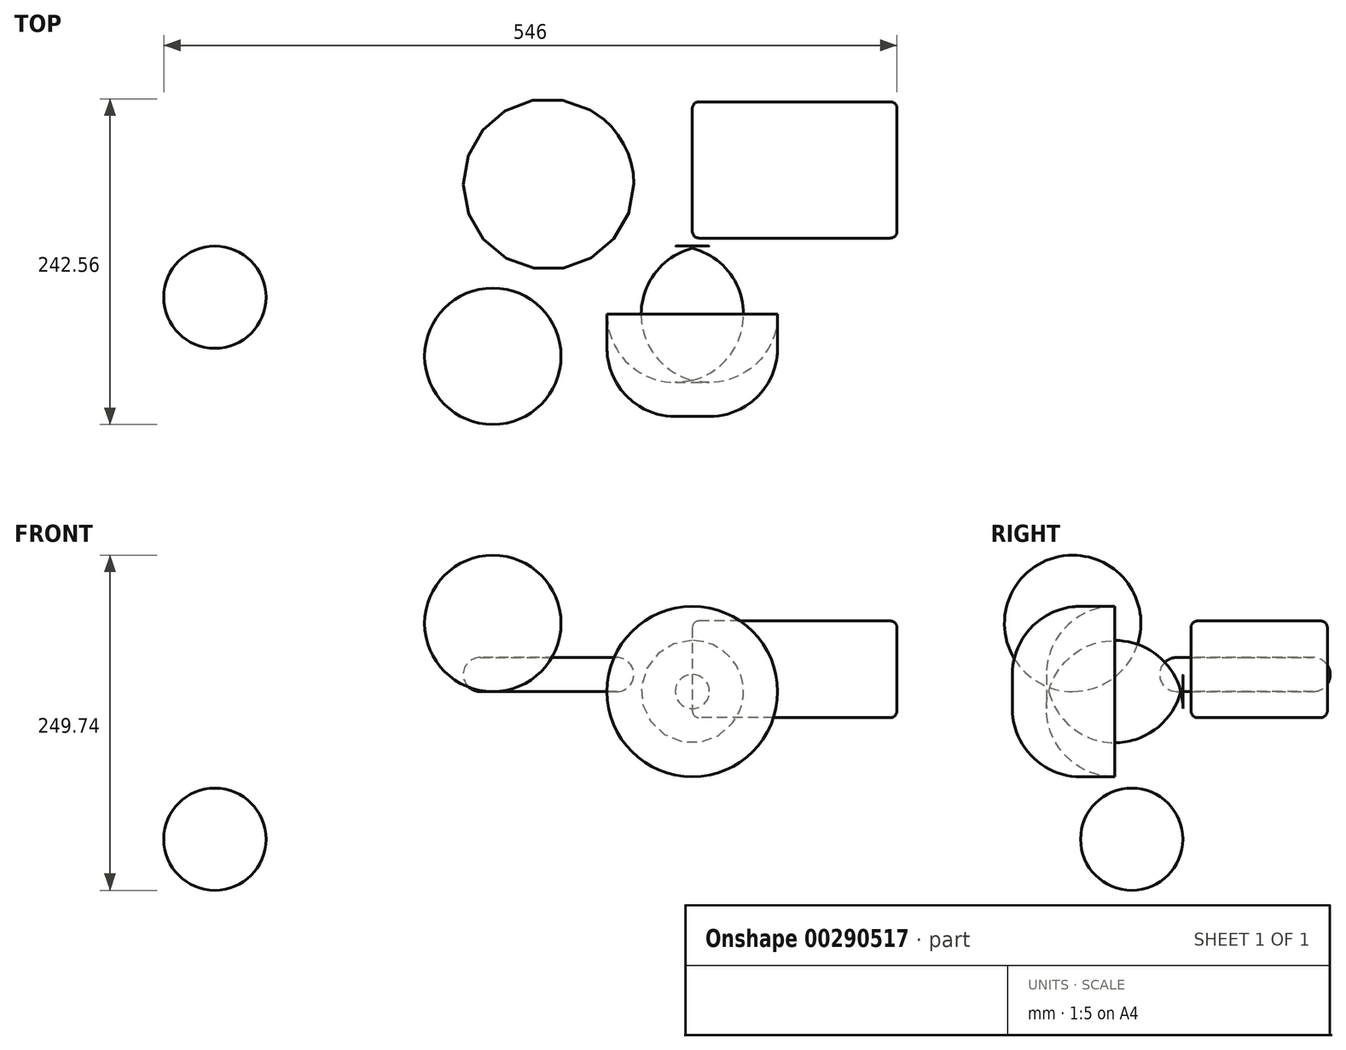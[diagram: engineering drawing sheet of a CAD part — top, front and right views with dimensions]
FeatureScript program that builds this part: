
annotation { "Feature Type Name" : "Feature", "Feature Type Description" : "" }
export const myFeature = defineFeature(function(context is Context, id is Id, definition is map)
    precondition{}
    {
        {
            var Q0;
            Q0=qCreatedBy(makeId("Front.planeOp"),FACE);
            var sketch = newSketch(context, id + "F0", { "sketchPlane" : qUnion([Q0])});
            skCircle(sketch, "E0", {"center": v(0, 0) * mm, "radius": 63.5 * mm});
            skSolve(sketch);
        }
        {
            var Q0;
            Q0=makeQuery(id+"F0.imprint","IMPRINT",FACE,{"disambiguationData":[TD([[makeQuery(id+"F0.imprint","IMPRINT",EDGE,{"derivedFrom":sQuery(id+"F0.wireOp",EDGE,"E0")}),1.0]])]});
            extrude(context, id + "F1", {"entities" : qUnion([Q0]), "depth" : 127 * mm});
        }
        {
            var Q0;
            Q0=makeQuery(id+"F1.opExtrude","CAP_FACE",FACE,{"disambiguationData":[OSD([sQuery(id+"F0.wireOp",EDGE,"E0")])],"isStart":false});
            fillet(context, id + "F2", {"entities" : qUnion([Q0]), "radius" : 50.8 * mm, "tangentPropagation" : true, "allowEdgeOverflow" : false});
        }
        {
            var Q0;
            Q0=makeQuery(id+"F1.opExtrude","CAP_FACE",FACE,{"disambiguationData":[OSD([sQuery(id+"F0.wireOp",EDGE,"E0")])],"isStart":true});
            fillet(context, id + "F3", {"entities" : qUnion([Q0]), "radius" : 50.8 * mm, "tangentPropagation" : true, "allowEdgeOverflow" : false});
        }
        {
            var Q0;
            Q0=qCreatedBy(makeId("Right.planeOp"),FACE);
            var sketch = newSketch(context, id + "F4", { "sketchPlane" : qUnion([Q0])});
            skLineSegment(sketch, "E1.bottom", {"start": v(5.96, 52.64) * mm, "end": v(107.56, 52.64) * mm});
            skLineSegment(sketch, "E1.top", {"start": v(5.96, -19.44) * mm, "end": v(107.56, -19.44) * mm});
            skLineSegment(sketch, "E1.left", {"start": v(5.96, 52.64) * mm, "end": v(5.96, -19.44) * mm});
            skLineSegment(sketch, "E1.right", {"start": v(107.56, 52.64) * mm, "end": v(107.56, -19.44) * mm});
            skSolve(sketch);
        }
        {
            var Q0;
            Q0=makeQuery(id+"F4.imprint","IMPRINT",FACE,{"disambiguationData":[TD([[makeQuery(id+"F4.imprint","IMPRINT",EDGE,{"derivedFrom":sQuery(id+"F4.wireOp",EDGE,"E1.bottom")}),-1.0]])]});
            extrude(context, id + "F5", {"entities" : qUnion([Q0]), "depth" : 152.4 * mm});
        }
        {
            var Q0;
            Q0=makeQuery(id+"F5.opExtrude","CAP_FACE",FACE,{"disambiguationData":[OSD([sQuery(id+"F4.wireOp",EDGE,"E1.bottom"),sQuery(id+"F4.wireOp",EDGE,"E1.top"),sQuery(id+"F4.wireOp",EDGE,"E1.left"),sQuery(id+"F4.wireOp",EDGE,"E1.right")])],"isStart":false});
            fillet(context, id + "F6", {"entities" : qUnion([Q0]), "radius" : 5.08 * mm, "tangentPropagation" : true, "allowEdgeOverflow" : false});
        }
        {
            var Q0;
            Q0=makeQuery(id+"F5.opExtrude","SWEPT_FACE",FACE,{"disambiguationData":[OSD([sQuery(id+"F4.wireOp",EDGE,"E1.bottom")])]});
            fillet(context, id + "F7", {"entities" : qUnion([Q0]), "radius" : 5.08 * mm, "tangentPropagation" : true, "allowEdgeOverflow" : false});
        }
        {
            var Q0;
            Q0=makeQuery(id+"F5.opExtrude","SWEPT_FACE",FACE,{"disambiguationData":[OSD([sQuery(id+"F4.wireOp",EDGE,"E1.left")])]});
            fillet(context, id + "F8", {"entities" : qUnion([Q0]), "radius" : 5.08 * mm, "tangentPropagation" : true, "allowEdgeOverflow" : false});
        }
        {
            var Q0;
            Q0=makeQuery(id+"F5.opExtrude","SWEPT_FACE",FACE,{"disambiguationData":[OSD([sQuery(id+"F4.wireOp",EDGE,"E1.top")])]});
            fillet(context, id + "F9", {"entities" : qUnion([Q0]), "radius" : 5.08 * mm, "tangentPropagation" : true, "allowEdgeOverflow" : false});
        }
        {
            var Q0;
            Q0=makeQuery(id+"F5.opExtrude","SWEPT_FACE",FACE,{"disambiguationData":[OSD([sQuery(id+"F4.wireOp",EDGE,"E1.right")])]});
            fillet(context, id + "F10", {"entities" : qUnion([Q0]), "radius" : 5.08 * mm, "tangentPropagation" : true, "allowEdgeOverflow" : false});
        }
        {
            var Q0;
            Q0=qCreatedBy(makeId("Top.planeOp"),FACE);
            var sketch = newSketch(context, id + "F11", { "sketchPlane" : qUnion([Q0])});
            skCircle(sketch, "E2", {"center": v(-107.1, 46.15) * mm, "radius": 63.5 * mm});
            skSolve(sketch);
        }
        {
            var Q0;
            Q0=makeQuery(id+"F11.imprint","IMPRINT",FACE,{"disambiguationData":[TD([[makeQuery(id+"F11.imprint","IMPRINT",EDGE,{"derivedFrom":sQuery(id+"F11.wireOp",EDGE,"E2")}),1.0]])]});
            extrude(context, id + "F12", {"entities" : qUnion([Q0]), "depth" : 25.4 * mm});
        }
        {
            var Q0;
            Q0=makeQuery(id+"F12.opExtrude","CAP_FACE",FACE,{"disambiguationData":[OSD([sQuery(id+"F11.wireOp",EDGE,"E2")])],"isStart":true});
            fillet(context, id + "F13", {"entities" : qUnion([Q0]), "radius" : 12.7 * mm, "tangentPropagation" : true, "allowEdgeOverflow" : false});
        }
        {
            var Q0;
            Q0=makeQuery(id+"F12.opExtrude","CAP_FACE",FACE,{"disambiguationData":[OSD([sQuery(id+"F11.wireOp",EDGE,"E2")])],"isStart":false});
            fillet(context, id + "F14", {"entities" : qUnion([Q0]), "radius" : 12.7 * mm, "tangentPropagation" : true, "allowEdgeOverflow" : false});
        }
        {
            var Q0;
            Q0=qCreatedBy(makeId("Top.planeOp"),FACE);
            var sketch = newSketch(context, id + "F15", { "sketchPlane" : qUnion([Q0])});
            skCircle(sketch, "E3", {"center": v(-148.55, -82.1) * mm, "radius": 50.8 * mm});
            skSolve(sketch);
        }
        {
            var Q0;
            Q0=makeQuery(id+"F15.imprint","IMPRINT",FACE,{"disambiguationData":[TD([[makeQuery(id+"F15.imprint","IMPRINT",EDGE,{"derivedFrom":sQuery(id+"F15.wireOp",EDGE,"E3")}),1.0]])]});
            extrude(context, id + "F16", {"entities" : qUnion([Q0]), "depth" : 101.6 * mm});
        }
        {
            var Q0;
            Q0=makeQuery(id+"F16.opExtrude","CAP_FACE",FACE,{"disambiguationData":[OSD([sQuery(id+"F15.wireOp",EDGE,"E3")])],"isStart":false});
            var Q1;
            Q1=makeQuery(id+"F16.opExtrude","SWEPT_FACE",FACE,{"disambiguationData":[OSD([sQuery(id+"F15.wireOp",EDGE,"E3")])]});
            fillet(context, id + "F17", {"entities" : qUnion([Q0, Q1]), "radius" : 50.8 * mm, "tangentPropagation" : true, "allowEdgeOverflow" : false});
        }
        {
            var Q0;
            Q0=qCreatedBy(makeId("Front.planeOp"),FACE);
            var sketch = newSketch(context, id + "F18", { "sketchPlane" : qUnion([Q0])});
            skCircle(sketch, "E4", {"center": v(-355.5, -110.04) * mm, "radius": 38.1 * mm});
            skSolve(sketch);
        }
        {
            var Q0;
            Q0=makeQuery(id+"F18.imprint","IMPRINT",FACE,{"disambiguationData":[TD([[makeQuery(id+"F18.imprint","IMPRINT",EDGE,{"derivedFrom":sQuery(id+"F18.wireOp",EDGE,"E4")}),1.0]])]});
            extrude(context, id + "F19", {"entities" : qUnion([Q0]), "depth" : 76.2 * mm});
        }
        {
            var Q0;
            Q0=makeQuery(id+"F19.opExtrude","CAP_FACE",FACE,{"disambiguationData":[OSD([sQuery(id+"F18.wireOp",EDGE,"E4")])],"isStart":false});
            var Q1;
            Q1=makeQuery(id+"F19.opExtrude","SWEPT_FACE",FACE,{"disambiguationData":[OSD([sQuery(id+"F18.wireOp",EDGE,"E4")])]});
            fillet(context, id + "F20", {"entities" : qUnion([Q0, Q1]), "radius" : 38.1 * mm, "tangentPropagation" : true, "allowEdgeOverflow" : false});
        }
    });
